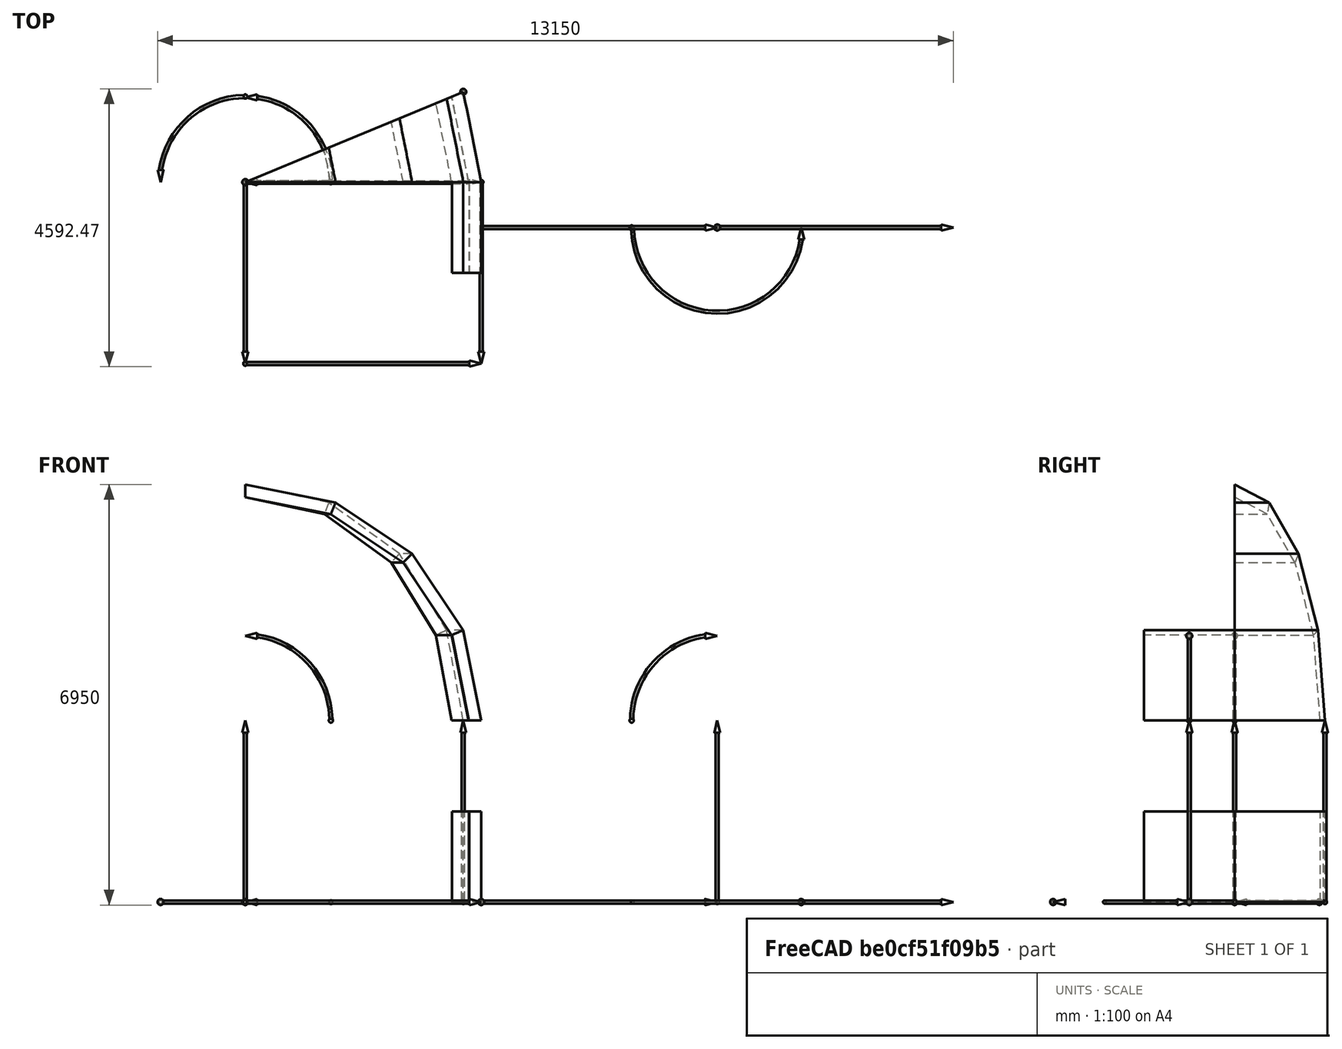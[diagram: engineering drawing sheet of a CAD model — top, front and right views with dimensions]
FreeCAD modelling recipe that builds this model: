
FCSTD DOCUMENT  (FreeCAD 0.18R16146 (Git))
Label: principle
License: CreativeCommons Attribution
LicenseURL: http://creativecommons.org/licenses/by/4.0/
objects: Part::Part2DObjectPython×176, Part::Feature×18, Part::Loft×7, Part::Cone×6, Part::MultiFuse×6, Part::RuledSurface×4, Part::Cylinder×4, Part::Sphere×4, Part::Sweep×2, Part::Box×2, Part::Cut×2
note: 231 computed .brp shape members not serialized (recipe doc carries the construction recipe); baked Part::Feature solids carry a one-line shape summary decoded from their .brp

FEATURE [Part::Part2DObjectPython] Line  # Draft 2D object (typed FeaturePython)
  ChamferSize = 0
  Closed = false
  End = (3900,0,1500)
  FilletRadius = 0
  Length = 1500
  MakeFace = false
  Points = (2) [(3900,0,0),(3900,0,1500)]
  Start = (3900,0,0)
  Subdivisions = 0
FEATURE [Part::Part2DObjectPython] Line001  # Draft 2D object (typed FeaturePython)
  ChamferSize = 0
  Closed = false
  End = (3603.13,0,4492.47)
  FilletRadius = 0
  Length = 1521.7
  MakeFace = false
  Points = (2) [(3900,0,3000),(3603.13,0,4492.47)]
  Start = (3900,0,3000)
  Subdivisions = 0
FEATURE [Part::Part2DObjectPython] Line002  # Draft 2D object (typed FeaturePython)
  ChamferSize = 0
  Closed = false
  End = (3696.08,0,1500)
  FilletRadius = 0
  Length = 1500
  MakeFace = false
  Points = (2) [(3696.08,0,0),(3696.08,0,1500)]
  Start = (3696.08,0,0)
  Subdivisions = 0
FEATURE [Part::Part2DObjectPython] Line003  # Draft 2D object (typed FeaturePython)
  ChamferSize = 0
  Closed = false
  End = (3414.73,0,4414.43)
  FilletRadius = 0
  Length = 1442.14
  MakeFace = false
  Points = (2) [(3696.08,0,3000),(3414.73,0,4414.43)]
  Start = (3696.08,0,3000)
  Subdivisions = 0
FEATURE [Part::Part2DObjectPython] Line004  # Draft 2D object (typed FeaturePython)
  ChamferSize = 0
  Closed = false
  End = (3700,0,1500)
  FilletRadius = 0
  Length = 1500
  MakeFace = false
  Points = (2) [(3700,0,0),(3700,0,1500)]
  Start = (3700,0,0)
  Subdivisions = 0
FEATURE [Part::Part2DObjectPython] Line005  # Draft 2D object (typed FeaturePython)
  ChamferSize = 0
  Closed = false
  End = (3411.04,0,4412.9)
  FilletRadius = 0
  Length = 1440.58
  MakeFace = false
  Points = (2) [(3692.09,0,3000),(3411.04,0,4412.9)]
  Start = (3692.09,0,3000)
  Subdivisions = 0
FEATURE [Part::Part2DObjectPython] Line010  # Draft 2D object (typed FeaturePython)
  ChamferSize = 0
  Closed = false
  End = (-200,-4.44e-14,0)
  FilletRadius = 0
  Length = 200
  MakeFace = false
  Placement = pos=(0,0,0) rot=(0,0,-1;1.5708rad)
  Points = (2) [(0,0,0),(0,-200,0)]
  Start = (0,0,0)
  Subdivisions = 0
FEATURE [Part::Part2DObjectPython] Line012  # Draft 2D object (typed FeaturePython)
  ChamferSize = 0
  Closed = false
  End = (0,-3200,0)
  FilletRadius = 0
  Length = 200
  MakeFace = false
  Placement = pos=(0,-3000,0) rot=(0,0,1;0rad)
  Points = (2) [(0,0,0),(0,-200,0)]
  Start = (0,-3000,0)
  Subdivisions = 0
FEATURE [Part::Part2DObjectPython] Line015  # Draft 2D object (typed FeaturePython)
  ChamferSize = 0
  Closed = false
  End = (-200,-3000,0)
  FilletRadius = 0
  Length = 200
  MakeFace = false
  Placement = pos=(0,-3000,0) rot=(0,0,-1;1.5708rad)
  Points = (2) [(0,0,0),(0,-200,0)]
  Start = (0,-3000,0)
  Subdivisions = 0
FEATURE [Part::RuledSurface] Surface
  Curve1 = -> Line001 [Edge1]
  Curve2 = -> Line003 [Edge1]
  Orientation = 0
FEATURE [Part::RuledSurface] Surface001
  Curve1 = -> Line001 [Edge1]
  Curve2 = -> Line005 [Edge1]
  Orientation = 0
FEATURE [Part::RuledSurface] Surface002
  Curve1 = -> Line [Edge1]
  Curve2 = -> Line002 [Edge1]
  Orientation = 0
FEATURE [Part::RuledSurface] Surface003
  Curve1 = -> Line [Edge1]
  Curve2 = -> Line004 [Edge1]
  Orientation = 0
FEATURE [Part::Feature] Surface004
  Placement = pos=(0,0,0) rot=(0,0,1;0.392699rad)
  shape: bbox 188.4 x 78.04 x 1500 mm, 1 faces, 0 solids (baked)
FEATURE [Part::Loft] Loft
  Closed = false
  MaxDegree = 5
  Ruled = false
  Sections = -> [Surface002,Surface004]
  Solid = true
FEATURE [Part::Feature] Surface005
  Placement = pos=(0,-1500,0) rot=(0,0,1;0rad)
  shape: bbox 200 x 2e-07 x 1500 mm, 1 faces, 0 solids (baked)
FEATURE [Part::Loft] Loft001
  Closed = false
  MaxDegree = 5
  Ruled = false
  Sections = -> [Surface003,Surface005]
  Solid = true
FEATURE [Part::Feature] Surface006
  Placement = pos=(1148.05,0,228.361) rot=(0,-1,0;0.392699rad)
  shape: bbox 992.4 x 2e-07 x 1345 mm, 1 faces, 0 solids (baked)
FEATURE [Part::Feature] Surface007
  Placement = pos=(2121.32,0,878.68) rot=(0,-1,0;0.785398rad)
  shape: bbox 1345 x 2e-07 x 992.4 mm, 1 faces, 0 solids (baked)
FEATURE [Part::Feature] Surface008
  Placement = pos=(2771.64,0,1851.95) rot=(0,-1,0;1.1781rad)
  shape: bbox 1492 x 2e-07 x 489 mm, 1 faces, 0 solids (baked)
FEATURE [Part::Feature] Surface009
  Placement = pos=(0,0,0) rot=(0,0,1;0.392699rad)
  shape: bbox 451.7 x 187.1 x 1492 mm, 1 faces, 0 solids (baked)
FEATURE [Part::Feature] Surface010
  Placement = pos=(1060.66,439.34,228.361) rot=(0.139281,-0.700215,0.700215;0.553564rad)
  shape: bbox 916.9 x 379.8 x 1345 mm, 1 faces, 0 solids (baked)
FEATURE [Part::Feature] Surface011
  Placement = pos=(1959.84,811.794,878.68) rot=(0.176494,-0.887296,0.426094;0.873518rad)
  shape: bbox 1242 x 514.6 x 992.4 mm, 1 faces, 0 solids (baked)
FEATURE [Part::Feature] Surface012
  Placement = pos=(2560.66,1060.66,1851.95) rot=(0.187271,-0.941476,0.280271;1.23443rad)
  shape: bbox 1379 x 571.1 x 489 mm, 1 faces, 0 solids (baked)
FEATURE [Part::Loft] Loft002
  Closed = false
  MaxDegree = 5
  Ruled = false
  Sections = -> [Surface001,Surface009]
  Solid = true
FEATURE [Part::Loft] Loft003
  Closed = false
  MaxDegree = 5
  Ruled = false
  Sections = -> [Surface006,Surface010]
  Solid = true
FEATURE [Part::Loft] Loft004
  Closed = false
  MaxDegree = 5
  Ruled = false
  Sections = -> [Surface007,Surface011]
  Solid = true
FEATURE [Part::Loft] Loft005
  Closed = false
  MaxDegree = 5
  Ruled = false
  Sections = -> [Surface008,Surface012]
  Solid = true
FEATURE [Part::Feature] Surface013
  Placement = pos=(0,-1500,0) rot=(0,0,1;0rad)
  shape: bbox 485.3 x 2e-07 x 1492 mm, 1 faces, 0 solids (baked)
FEATURE [Part::Loft] Loft006
  Closed = false
  MaxDegree = 5
  Ruled = false
  Sections = -> [Surface,Surface013]
  Solid = true
FEATURE [Part::Part2DObjectPython] Rectangle  # Draft 2D object (typed FeaturePython)
  ChamferSize = 0
  Columns = 1
  FilletRadius = 0
  Height = 1500
  Length = 1500
  MakeFace = false
  Placement = pos=(3900,-1500,0) rot=(0.57735,0.57735,0.57735;2.0944rad)
  Rows = 1
FEATURE [Part::Part2DObjectPython] Rectangle001  # Draft 2D object (typed FeaturePython)
  ChamferSize = 0
  Columns = 1
  FilletRadius = 0
  Height = 1500
  Length = 1500
  MakeFace = false
  Placement = pos=(3700,-1500,0) rot=(0.57735,0.57735,0.57735;2.0944rad)
  Rows = 1
FEATURE [Part::Part2DObjectPython] Line016  # Draft 2D object (typed FeaturePython)
  ChamferSize = 0
  Closed = false
  End = (3900,-1500,0)
  FilletRadius = 0
  Length = 200
  MakeFace = true
  Placement = pos=(3700,-1500,0) rot=(0.57735,0.57735,0.57735;2.0944rad)
  Points = (2) [(0,0,0),(0,0,200)]
  Start = (3700,-1500,0)
  Subdivisions = 0
  Support = -> [Loft]
FEATURE [Part::Part2DObjectPython] Line017  # Draft 2D object (typed FeaturePython)
  ChamferSize = 0
  Closed = false
  End = (3900,-1500,1500)
  FilletRadius = 0
  Length = 200
  MakeFace = true
  Placement = pos=(3700,-1500,1500) rot=(0.57735,0.57735,0.57735;2.0944rad)
  Points = (2) [(0,0,0),(0,0,200)]
  Start = (3700,-1500,1500)
  Subdivisions = 0
FEATURE [Part::Part2DObjectPython] Wire001  # Draft 2D object (typed FeaturePython)
  ChamferSize = 0
  Closed = true
  End = (3696.08,0,3000)
  FilletRadius = 0
  Length = 5883.51
  MakeFace = false
  Placement = pos=(3411.04,0,4412.9) rot=(0.57735,0.57735,0.57735;2.0944rad)
  Points = (4) [(0,0,0),(-1500,1.52882,3.69089),(-1500,-1412.9,285.038),(0,-1412.9,285.038)]
  Start = (3411.04,0,4412.9)
  Subdivisions = 0
FEATURE [Part::Part2DObjectPython] Line018  # Draft 2D object (typed FeaturePython)
  ChamferSize = 0
  Closed = false
  End = (3603.13,-1500,4492.47)
  FilletRadius = 0
  Length = 203.918
  MakeFace = true
  Placement = pos=(3414.73,-1500,4414.43) rot=(0.57735,0.57735,0.57735;2.0944rad)
  Points = (2) [(0,0,0),(0,78.0361,188.396)]
  Start = (3414.73,-1500,4414.43)
  Subdivisions = 0
  Support = -> [Loft006]
FEATURE [Part::Part2DObjectPython] Line019  # Draft 2D object (typed FeaturePython)
  ChamferSize = 0
  Closed = false
  End = (3900,-1500,3000)
  FilletRadius = 0
  Length = 203.918
  MakeFace = true
  Placement = pos=(3696.08,-1500,3000) rot=(0.57735,0.57735,0.57735;2.0944rad)
  Points = (2) [(0,0,0),(0,0,203.918)]
  Start = (3696.08,-1500,3000)
  Subdivisions = 0
FEATURE [Part::Cylinder] Cylinder  label="Цилиндр"
  Angle = 360
  AttacherType = Attacher::AttachEngine3D
  Height = 3700
  Placement = pos=(0,0,0) rot=(0,1,0;1.5708rad)
  Radius = 25
FEATURE [Part::Sphere] Sphere  label="Сфера"
  Angle1 = -90
  Angle2 = 90
  Angle3 = 360
  AttacherType = Attacher::AttachEngine3D
  Radius = 35
FEATURE [Part::Cone] Cone  label="Конус"
  Angle = 360
  AttacherType = Attacher::AttachEngine3D
  Height = 200
  Placement = pos=(3700,0,0) rot=(0,1,0;1.5708rad)
  Radius1 = 50
  Radius2 = 0
FEATURE [Part::MultiFuse] Fusion  label="OR"
  Placement = pos=(0,0,-4.17e-13) rot=(0,0,1;0rad)
  Refine = true
  Shapes = -> [Cylinder,Sphere,Cone]
FEATURE [Part::Cone] Cone001  label="Конус001"
  Angle = 360
  AttacherType = Attacher::AttachEngine3D
  Height = 200
  Placement = pos=(2800,0,0) rot=(0,1,0;1.5708rad)
  Radius1 = 50
  Radius2 = 0
FEATURE [Part::Sphere] Sphere001  label="Сфера001"
  Angle1 = -90
  Angle2 = 90
  Angle3 = 360
  AttacherType = Attacher::AttachEngine3D
  Radius = 35
FEATURE [Part::Cylinder] Cylinder001  label="Цилиндр001"
  Angle = 360
  AttacherType = Attacher::AttachEngine3D
  Height = 2800
  Placement = pos=(0,0,0) rot=(0,1,0;1.5708rad)
  Radius = 25
FEATURE [Part::MultiFuse] Fusion001  label="H1"
  Placement = pos=(3603.13,1492.47,0) rot=(0.19148,-0.962637,0.19148;1.60887rad)
  Refine = true
  Shapes = -> [Cylinder001,Sphere001,Cone001]
FEATURE [Part::Cone] Cone002  label="Конус002"
  Angle = 360
  AttacherType = Attacher::AttachEngine3D
  Height = 200
  Placement = pos=(2800,0,0) rot=(0,1,0;1.5708rad)
  Radius1 = 50
  Radius2 = 0
FEATURE [Part::Sphere] Sphere002  label="Сфера002"
  Angle1 = -90
  Angle2 = 90
  Angle3 = 360
  AttacherType = Attacher::AttachEngine3D
  Radius = 35
FEATURE [Part::Cylinder] Cylinder002  label="Цилиндр002"
  Angle = 360
  AttacherType = Attacher::AttachEngine3D
  Height = 2800
  Placement = pos=(0,0,0) rot=(0,1,0;1.5708rad)
  Radius = 25
FEATURE [Part::MultiFuse] Fusion002  label="LONG"
  Placement = pos=(0,0,0) rot=(0,0,-1;1.5708rad)
  Refine = true
  Shapes = -> [Cylinder002,Sphere002,Cone002]
FEATURE [Part::Sphere] Sphere003  label="Сфера003"
  Angle1 = -90
  Angle2 = 90
  Angle3 = 360
  AttacherType = Attacher::AttachEngine3D
  Placement = pos=(1415,0,0) rot=(0,0,1;0rad)
  Radius = 35
FEATURE [Part::Part2DObjectPython] Circle001  # Draft 2D object (typed FeaturePython)
  FirstAngle = 0
  LastAngle = 0
  MakeFace = true
  Placement = pos=(1415,0,0) rot=(1,0,0;1.5708rad)
  Radius = 25
FEATURE [Part::Part2DObjectPython] Arc  # Draft 2D object (typed FeaturePython)
  FirstAngle = 0
  LastAngle = 90
  MakeFace = true
  Radius = 1415
FEATURE [Part::Sweep] Sweep
  Frenet = false
  Sections = -> [Circle001]
  Solid = true
  Spine = -> Arc [Edge1]
  Transition = 1
FEATURE [Part::Cone] Cone003  label="Конус003"
  Angle = 360
  AttacherType = Attacher::AttachEngine3D
  Height = 200
  Placement = pos=(200,1400,0) rot=(0,-1,0;1.5708rad)
  Radius1 = 50
  Radius2 = 0
FEATURE [Part::Feature] Fusion004  label="H002"
  Placement = pos=(0,0,0) rot=(0.19148,-0.962637,0.19148;1.60887rad)
  shape: bbox 100 x 100 x 3035 mm, 4 faces (baked)
FEATURE [Part::Feature] Fusion006  label="OR001"
  Placement = pos=(0,-3000,-4.17e-13) rot=(0,0,1;0rad)
  shape: bbox 3935 x 100 x 100 mm, 4 faces (baked)
FEATURE [Part::Feature] Fusion007  label="LONG001"
  Placement = pos=(3900,0,0) rot=(0,0,-1;1.5708rad)
  shape: bbox 100 x 3035 x 100 mm, 4 faces (baked)
FEATURE [Part::Part2DObjectPython] Line021  # Draft 2D object (typed FeaturePython)
  ChamferSize = 0
  Closed = false
  End = (3900,0,3000)
  FilletRadius = 0
  Length = 3900
  MakeFace = true
  Placement = pos=(6.251e-13,-3.501e-13,3000) rot=(0,0,1;0rad)
  Points = (2) [(0,0,0),(3900,2.30658e-13,4.54747e-13)]
  Start = (6.251e-13,-3.501e-13,3000)
  Subdivisions = 0
FEATURE [Part::Part2DObjectPython] Line025  # Draft 2D object (typed FeaturePython)
  ChamferSize = 0
  Closed = false
  End = (3900,0,0)
  FilletRadius = 0
  Length = 3000
  MakeFace = true
  Placement = pos=(3900,0,3000) rot=(0,0,1;0rad)
  Points = (2) [(0,0,0),(0,0,-3000)]
  Start = (3900,0,3000)
  Subdivisions = 0
FEATURE [Part::Part2DObjectPython] Line026  # Draft 2D object (typed FeaturePython)
  ChamferSize = 0
  Closed = false
  End = (3603.13,1492.47,0)
  FilletRadius = 0
  Length = 1521.7
  MakeFace = true
  Placement = pos=(3900,0,0) rot=(0,0,1;0rad)
  Points = (2) [(0,0,0),(-296.87,1492.47,0)]
  Start = (3900,0,0)
  Subdivisions = 0
  Support = -> [Loft]
FEATURE [Part::Part2DObjectPython] Line027  # Draft 2D object (typed FeaturePython)
  ChamferSize = 0
  Closed = false
  End = (2757.72,2757.72,0)
  FilletRadius = 0
  Length = 1521.7
  MakeFace = true
  Placement = pos=(3603.13,1492.47,0) rot=(0,0,1;0.392699rad)
  Points = (2) [(0,0,0),(-296.87,1492.47,0)]
  Start = (3603.13,1492.47,0)
  Subdivisions = 0
  Support = -> [Loft]
FEATURE [Part::Part2DObjectPython] Line028  # Draft 2D object (typed FeaturePython)
  ChamferSize = 0
  Closed = false
  End = (1492.47,3603.13,0)
  FilletRadius = 0
  Length = 1521.7
  MakeFace = true
  Placement = pos=(2757.72,2757.72,0) rot=(0,0,1;0.785398rad)
  Points = (2) [(0,0,0),(-296.87,1492.47,0)]
  Start = (2757.72,2757.72,0)
  Subdivisions = 0
  Support = -> [Loft]
FEATURE [Part::Part2DObjectPython] Line029  # Draft 2D object (typed FeaturePython)
  ChamferSize = 0
  Closed = false
  End = (-4.3201e-12,3900,0)
  FilletRadius = 0
  Length = 1521.7
  MakeFace = true
  Placement = pos=(1492.47,3603.13,0) rot=(0,0,1;1.1781rad)
  Points = (2) [(0,0,0),(-296.87,1492.47,0)]
  Start = (1492.47,3603.13,0)
  Subdivisions = 0
  Support = -> [Loft]
FEATURE [Part::Box] Box  label="Куб"
  AttacherType = Attacher::AttachEngine3D
  Height = 60
  Length = 200
  Placement = pos=(0,1300,-30) rot=(0,0,1;0rad)
  Width = 200
FEATURE [Part::Cut] Cut
  Base = -> Sweep
  Refine = true
  Tool = -> Box
FEATURE [Part::MultiFuse] Fusion010  label="TORSION"
  Refine = true
  Shapes = -> [Cut,Sphere003,Cone003]
FEATURE [Part::Part2DObjectPython] Line030  # Draft 2D object (typed FeaturePython)
  ChamferSize = 0
  Closed = false
  End = (3603.13,1492.47,0)
  FilletRadius = 0
  Length = 3900
  MakeFace = true
  Points = (2) [(0,0,0),(3603.13,1492.47,0)]
  Start = (0,0,0)
  Subdivisions = 0
FEATURE [Part::Part2DObjectPython] Line031  # Draft 2D object (typed FeaturePython)
  ChamferSize = 0
  Closed = false
  End = (2757.72,2757.72,0)
  FilletRadius = 0
  Length = 3900
  MakeFace = true
  Placement = pos=(0,0,0) rot=(0,0,1;0.392699rad)
  Points = (2) [(0,0,0),(3603.13,1492.47,0)]
  Start = (0,0,0)
  Subdivisions = 0
FEATURE [Part::Part2DObjectPython] Line032  # Draft 2D object (typed FeaturePython)
  ChamferSize = 0
  Closed = false
  End = (1492.47,3603.13,0)
  FilletRadius = 0
  Length = 3900
  MakeFace = true
  Placement = pos=(0,0,0) rot=(0,0,1;0.785398rad)
  Points = (2) [(0,0,0),(3603.13,1492.47,0)]
  Start = (0,0,0)
  Subdivisions = 0
FEATURE [Part::Part2DObjectPython] Line033  # Draft 2D object (typed FeaturePython)
  ChamferSize = 0
  Closed = false
  End = (3603.13,-1.193e-13,4492.47)
  FilletRadius = 0
  Length = 3900
  MakeFace = true
  Placement = pos=(9.09e-13,-3.5e-13,3000) rot=(0,-1,0;0.392699rad)
  Points = (2) [(0,0,0),(3900,2.30658e-13,2.27374e-12)]
  Start = (9.09e-13,-3.5e-13,3000)
  Subdivisions = 0
FEATURE [Part::Part2DObjectPython] Line034  # Draft 2D object (typed FeaturePython)
  ChamferSize = 0
  Closed = false
  End = (2757.72,-1.193e-13,5757.72)
  FilletRadius = 0
  Length = 3900
  MakeFace = true
  Placement = pos=(9.09e-13,-3.5e-13,3000) rot=(0,-1,0;0.785398rad)
  Points = (2) [(0,0,0),(3900,2.30658e-13,-4.54747e-13)]
  Start = (9.09e-13,-3.5e-13,3000)
  Subdivisions = 0
FEATURE [Part::Part2DObjectPython] Line035  # Draft 2D object (typed FeaturePython)
  ChamferSize = 0
  Closed = false
  End = (2757.72,-1.193e-13,5757.72)
  FilletRadius = 0
  Length = 3900
  MakeFace = true
  Placement = pos=(6.82e-13,-3.5e-13,3000) rot=(0,-1,0;1.1781rad)
  Points = (2) [(-2.27374e-12,-1e-16,4.54747e-13),(3603.13,2.30658e-13,-1492.47)]
  Start = (-3.982e-13,-3.501e-13,3000)
  Subdivisions = 0
FEATURE [Part::Feature] Fusion011  label="TORSION001"
  Placement = pos=(6.251e-13,-3.501e-13,3000) rot=(1,0,0;1.5708rad)
  shape: bbox 1558 x 100 x 1579 mm, 4 faces (baked)
FEATURE [Part::Feature] Fusion012  label="TORSION002"
  Placement = pos=(0,0,0) rot=(0,0,1;1.5708rad)
  shape: bbox 1579 x 1558 x 100 mm, 4 faces (baked)
FEATURE [Part::Part2DObjectPython] Line036  # Draft 2D object (typed FeaturePython)
  ChamferSize = 0
  Closed = false
  End = (2757.72,-1.193e-13,5757.72)
  FilletRadius = 0
  Length = 3900
  MakeFace = true
  Placement = pos=(9.09e-13,-3.5e-13,3000) rot=(0,-1,0;0.785398rad)
  Points = (2) [(0,0,0),(3900,2.30658e-13,3.18323e-12)]
  Start = (9.09e-13,-3.5e-13,3000)
  Subdivisions = 0
FEATURE [Part::Part2DObjectPython] Line037  # Draft 2D object (typed FeaturePython)
  ChamferSize = 0
  Closed = false
  End = (1492.47,-1.193e-13,6603.13)
  FilletRadius = 0
  Length = 3900
  MakeFace = true
  Placement = pos=(9.09e-13,-3.5e-13,3000) rot=(0,-1,0;1.1781rad)
  Points = (2) [(0,0,0),(3900,2.30658e-13,3.41061e-12)]
  Start = (9.09e-13,-3.5e-13,3000)
  Subdivisions = 0
FEATURE [Part::Part2DObjectPython] Line038  # Draft 2D object (typed FeaturePython)
  ChamferSize = 0
  Closed = false
  End = (-2.0896e-12,-1.193e-13,6900)
  FilletRadius = 0
  Length = 3900
  MakeFace = true
  Placement = pos=(4.55e-13,-3.5e-13,3000) rot=(0,-1,0;1.5708rad)
  Points = (2) [(0,0,0),(3900,2.30658e-13,3.41061e-12)]
  Start = (4.55e-13,-3.5e-13,3000)
  Subdivisions = 0
FEATURE [Part::Part2DObjectPython] Line039  # Draft 2D object (typed FeaturePython)
  ChamferSize = 0
  Closed = false
  End = (-1.5916e-12,3900,0)
  FilletRadius = 0
  Length = 3900
  MakeFace = true
  Placement = pos=(0,0,0) rot=(0,0,1;1.1781rad)
  Points = (2) [(0,0,0),(3603.13,1492.47,0)]
  Start = (0,0,0)
  Subdivisions = 0
FEATURE [Part::Part2DObjectPython] Line040  # Draft 2D object (typed FeaturePython)
  ChamferSize = 0
  Closed = false
  End = (3900,0,1500)
  FilletRadius = 0
  Length = 1500
  MakeFace = false
  Points = (2) [(3900,0,0),(3900,0,1500)]
  Start = (3900,0,0)
  Subdivisions = 0
FEATURE [Part::Part2DObjectPython] Line041  # Draft 2D object (typed FeaturePython)
  ChamferSize = 0
  Closed = false
  End = (4196.87,0,4492.47)
  FilletRadius = 0
  Length = 1521.7
  MakeFace = false
  Points = (2) [(3900,0,3000),(4196.87,0,4492.47)]
  Start = (3900,0,3000)
  Subdivisions = 0
FEATURE [Part::Part2DObjectPython] Line042  # Draft 2D object (typed FeaturePython)
  ChamferSize = 0
  Closed = false
  End = (4103.92,0,1500)
  FilletRadius = 0
  Length = 1500
  MakeFace = false
  Points = (2) [(4103.92,0,0),(4103.92,0,1500)]
  Start = (4103.92,0,0)
  Subdivisions = 0
FEATURE [Part::Part2DObjectPython] Line043  # Draft 2D object (typed FeaturePython)
  ChamferSize = 0
  Closed = false
  End = (4385.27,0,4414.43)
  FilletRadius = 0
  Length = 1442.14
  MakeFace = false
  Points = (2) [(4103.92,0,3000),(4385.27,0,4414.43)]
  Start = (4103.92,0,3000)
  Subdivisions = 0
FEATURE [Part::Part2DObjectPython] Line044  # Draft 2D object (typed FeaturePython)
  ChamferSize = 0
  Closed = false
  End = (4100,0,1500)
  FilletRadius = 0
  Length = 1500
  MakeFace = false
  Points = (2) [(4100,0,0),(4100,0,1500)]
  Start = (4100,0,0)
  Subdivisions = 0
FEATURE [Part::Part2DObjectPython] Line045  # Draft 2D object (typed FeaturePython)
  ChamferSize = 0
  Closed = false
  End = (4388.96,0,4412.9)
  FilletRadius = 0
  Length = 1440.58
  MakeFace = false
  Points = (2) [(4107.91,0,3000),(4388.96,0,4412.9)]
  Start = (4107.91,0,3000)
  Subdivisions = 0
FEATURE [Part::Part2DObjectPython] Line056  # Draft 2D object (typed FeaturePython)
  ChamferSize = 0
  Closed = false
  End = (11700,0,1500)
  FilletRadius = 0
  Length = 1500
  MakeFace = false
  Points = (2) [(11700,0,0),(11700,0,1500)]
  Start = (11700,0,0)
  Subdivisions = 0
FEATURE [Part::Part2DObjectPython] Line057  # Draft 2D object (typed FeaturePython)
  ChamferSize = 0
  Closed = false
  End = (11403.1,0,4492.47)
  FilletRadius = 0
  Length = 1521.7
  MakeFace = false
  Points = (2) [(11700,0,3000),(11403.1,0,4492.47)]
  Start = (11700,0,3000)
  Subdivisions = 0
FEATURE [Part::Part2DObjectPython] Line058  # Draft 2D object (typed FeaturePython)
  ChamferSize = 0
  Closed = false
  End = (11496.1,0,1500)
  FilletRadius = 0
  Length = 1500
  MakeFace = false
  Points = (2) [(11496.1,0,0),(11496.1,0,1500)]
  Start = (11496.1,0,0)
  Subdivisions = 0
FEATURE [Part::Part2DObjectPython] Line059  # Draft 2D object (typed FeaturePython)
  ChamferSize = 0
  Closed = false
  End = (11214.7,0,4414.43)
  FilletRadius = 0
  Length = 1442.14
  MakeFace = false
  Points = (2) [(11496.1,0,3000),(11214.7,0,4414.43)]
  Start = (11496.1,0,3000)
  Subdivisions = 0
FEATURE [Part::Part2DObjectPython] Line060  # Draft 2D object (typed FeaturePython)
  ChamferSize = 0
  Closed = false
  End = (11500,0,1500)
  FilletRadius = 0
  Length = 1500
  MakeFace = false
  Points = (2) [(11500,0,0),(11500,0,1500)]
  Start = (11500,0,0)
  Subdivisions = 0
FEATURE [Part::Part2DObjectPython] Line061  # Draft 2D object (typed FeaturePython)
  ChamferSize = 0
  Closed = false
  End = (11211,0,4412.9)
  FilletRadius = 0
  Length = 1440.58
  MakeFace = false
  Points = (2) [(11492.1,0,3000),(11211,0,4412.9)]
  Start = (11492.1,0,3000)
  Subdivisions = 0
FEATURE [Part::Part2DObjectPython] Line062  # Draft 2D object (typed FeaturePython)
  ChamferSize = 0
  Closed = false
  End = (4196.87,-1500,4492.47)
  FilletRadius = 0
  Length = 1521.7
  MakeFace = false
  Placement = pos=(0,-1500,0) rot=(0,0,1;0rad)
  Points = (2) [(3900,0,3000),(4196.87,0,4492.47)]
  Start = (3900,-1500,3000)
  Subdivisions = 0
FEATURE [Part::Part2DObjectPython] Line063  # Draft 2D object (typed FeaturePython)
  ChamferSize = 0
  Closed = false
  End = (11403.1,-1500,4492.47)
  FilletRadius = 0
  Length = 1521.7
  MakeFace = false
  Placement = pos=(0,-1500,0) rot=(0,0,1;0rad)
  Points = (2) [(11700,0,3000),(11403.1,0,4492.47)]
  Start = (11700,-1500,3000)
  Subdivisions = 0
FEATURE [Part::Part2DObjectPython] Line064  # Draft 2D object (typed FeaturePython)
  ChamferSize = 0
  Closed = false
  End = (4385.27,-1500,4414.43)
  FilletRadius = 0
  Length = 1442.14
  MakeFace = false
  Placement = pos=(0,-1500,0) rot=(0,0,1;0rad)
  Points = (2) [(4103.92,0,3000),(4385.27,0,4414.43)]
  Start = (4103.92,-1500,3000)
  Subdivisions = 0
FEATURE [Part::Part2DObjectPython] Line065  # Draft 2D object (typed FeaturePython)
  ChamferSize = 0
  Closed = false
  End = (11214.7,-1500,4414.43)
  FilletRadius = 0
  Length = 1442.14
  MakeFace = false
  Placement = pos=(0,-1500,0) rot=(0,0,1;0rad)
  Points = (2) [(11496.1,0,3000),(11214.7,0,4414.43)]
  Start = (11496.1,-1500,3000)
  Subdivisions = 0
FEATURE [Part::Part2DObjectPython] Line066  # Draft 2D object (typed FeaturePython)
  ChamferSize = 0
  Closed = false
  End = (4100,-1500,1500)
  FilletRadius = 0
  Length = 1500
  MakeFace = false
  Placement = pos=(0,-1500,0) rot=(0,0,1;0rad)
  Points = (2) [(4100,0,0),(4100,0,1500)]
  Start = (4100,-1500,0)
  Subdivisions = 0
FEATURE [Part::Part2DObjectPython] Line067  # Draft 2D object (typed FeaturePython)
  ChamferSize = 0
  Closed = false
  End = (11700,-1500,1500)
  FilletRadius = 0
  Length = 1500
  MakeFace = false
  Placement = pos=(0,-1500,0) rot=(0,0,1;0rad)
  Points = (2) [(11700,0,0),(11700,0,1500)]
  Start = (11700,-1500,0)
  Subdivisions = 0
FEATURE [Part::Part2DObjectPython] Line068  # Draft 2D object (typed FeaturePython)
  ChamferSize = 0
  Closed = false
  End = (11500,-1500,1500)
  FilletRadius = 0
  Length = 1500
  MakeFace = false
  Placement = pos=(0,-1500,0) rot=(0,0,1;0rad)
  Points = (2) [(11500,0,0),(11500,0,1500)]
  Start = (11500,-1500,0)
  Subdivisions = 0
FEATURE [Part::Part2DObjectPython] Line069  # Draft 2D object (typed FeaturePython)
  ChamferSize = 0
  Closed = false
  End = (3900,-1500,1500)
  FilletRadius = 0
  Length = 200
  MakeFace = true
  Placement = pos=(4100,-1500,1500) rot=(0,0,1;0rad)
  Points = (2) [(0,0,0),(-200,0,0)]
  Start = (4100,-1500,1500)
  Subdivisions = 0
FEATURE [Part::Part2DObjectPython] Line070  # Draft 2D object (typed FeaturePython)
  ChamferSize = 0
  Closed = false
  End = (3900,-1500,0)
  FilletRadius = 0
  Length = 200
  MakeFace = true
  Placement = pos=(4100,-1500,0) rot=(0,0,1;0rad)
  Points = (2) [(0,0,0),(-200,0,0)]
  Start = (4100,-1500,0)
  Subdivisions = 0
FEATURE [Part::Part2DObjectPython] Line071  # Draft 2D object (typed FeaturePython)
  ChamferSize = 0
  Closed = false
  End = (4100,0,0)
  FilletRadius = 0
  Length = 1500
  MakeFace = true
  Placement = pos=(4100,-1500,0) rot=(0,0,1;0rad)
  Points = (2) [(0,0,0),(0,1500,0)]
  Start = (4100,-1500,0)
  Subdivisions = 0
FEATURE [Part::Part2DObjectPython] Line072  # Draft 2D object (typed FeaturePython)
  ChamferSize = 0
  Closed = false
  End = (4100,0,1500)
  FilletRadius = 0
  Length = 1500
  MakeFace = true
  Placement = pos=(4100,-1500,1500) rot=(0,0,1;0rad)
  Points = (2) [(0,0,0),(0,1500,0)]
  Start = (4100,-1500,1500)
  Subdivisions = 0
FEATURE [Part::Part2DObjectPython] Line073  # Draft 2D object (typed FeaturePython)
  ChamferSize = 0
  Closed = false
  End = (3900,0,1500)
  FilletRadius = 0
  Length = 200
  MakeFace = true
  Placement = pos=(4100,0,1500) rot=(0,0,1;0rad)
  Points = (2) [(0,0,0),(-200,6.12323e-15,0)]
  Start = (4100,0,1500)
  Subdivisions = 0
FEATURE [Part::Part2DObjectPython] Line074  # Draft 2D object (typed FeaturePython)
  ChamferSize = 0
  Closed = false
  End = (11700,0,1500)
  FilletRadius = 0
  Length = 1500
  MakeFace = true
  Placement = pos=(11700,-1500,1500) rot=(0,0,1;0rad)
  Points = (2) [(0,0,0),(0,1500,0)]
  Start = (11700,-1500,1500)
  Subdivisions = 0
FEATURE [Part::Part2DObjectPython] Line075  # Draft 2D object (typed FeaturePython)
  ChamferSize = 0
  Closed = false
  End = (11500,0,1500)
  FilletRadius = 0
  Length = 1500
  MakeFace = true
  Placement = pos=(11500,-1500,1500) rot=(0,0,1;0rad)
  Points = (2) [(0,0,0),(0,1500,0)]
  Start = (11500,-1500,1500)
  Subdivisions = 0
FEATURE [Part::Part2DObjectPython] Line076  # Draft 2D object (typed FeaturePython)
  ChamferSize = 0
  Closed = false
  End = (11700,0,0)
  FilletRadius = 0
  Length = 1500
  MakeFace = true
  Placement = pos=(11700,-1500,0) rot=(0,0,1;0rad)
  Points = (2) [(0,0,0),(0,1500,0)]
  Start = (11700,-1500,0)
  Subdivisions = 0
FEATURE [Part::Part2DObjectPython] Line077  # Draft 2D object (typed FeaturePython)
  ChamferSize = 0
  Closed = false
  End = (11500,0,0)
  FilletRadius = 0
  Length = 1500
  MakeFace = true
  Placement = pos=(11500,-1500,0) rot=(0,0,1;0rad)
  Points = (2) [(0,0,0),(0,1500,0)]
  Start = (11500,-1500,0)
  Subdivisions = 0
FEATURE [Part::Part2DObjectPython] Line078  # Draft 2D object (typed FeaturePython)
  ChamferSize = 0
  Closed = false
  End = (11700,0,1500)
  FilletRadius = 0
  Length = 200
  MakeFace = true
  Placement = pos=(11500,0,1500) rot=(0,0,1;0rad)
  Points = (2) [(0,0,0),(200,-6.12323e-15,0)]
  Start = (11500,0,1500)
  Subdivisions = 0
FEATURE [Part::Part2DObjectPython] Line079  # Draft 2D object (typed FeaturePython)
  ChamferSize = 0
  Closed = false
  End = (11500,-1500,1500)
  FilletRadius = 0
  Length = 200
  MakeFace = true
  Placement = pos=(11700,-1500,1500) rot=(0,0,1;0rad)
  Points = (2) [(0,0,0),(-200,0,0)]
  Start = (11700,-1500,1500)
  Subdivisions = 0
FEATURE [Part::Part2DObjectPython] Line080  # Draft 2D object (typed FeaturePython)
  ChamferSize = 0
  Closed = false
  End = (11500,-1500,0)
  FilletRadius = 0
  Length = 200
  MakeFace = true
  Placement = pos=(11700,-1500,0) rot=(0,0,1;0rad)
  Points = (2) [(0,0,0),(-200,0,0)]
  Start = (11700,-1500,0)
  Subdivisions = 0
FEATURE [Part::Part2DObjectPython] Line081  # Draft 2D object (typed FeaturePython)
  ChamferSize = 0
  Closed = false
  End = (11500,0,0)
  FilletRadius = 0
  Length = 200
  MakeFace = true
  Placement = pos=(11700,0,0) rot=(0,0,1;0rad)
  Points = (2) [(0,0,0),(-200,6.12323e-15,0)]
  Start = (11700,0,0)
  Subdivisions = 0
FEATURE [Part::Part2DObjectPython] Line082  # Draft 2D object (typed FeaturePython)
  ChamferSize = 0
  Closed = false
  End = (11403.1,0,4492.47)
  FilletRadius = 0
  Length = 1500
  MakeFace = true
  Placement = pos=(11403.1,-1500,4492.47) rot=(0,0,1;0rad)
  Points = (2) [(0,0,0),(0,1500,0)]
  Start = (11403.1,-1500,4492.47)
  Subdivisions = 0
FEATURE [Part::Part2DObjectPython] Line083  # Draft 2D object (typed FeaturePython)
  ChamferSize = 0
  Closed = false
  End = (11700,0,3000)
  FilletRadius = 0
  Length = 1500
  MakeFace = true
  Placement = pos=(11700,-1500,3000) rot=(0,0,1;0rad)
  Points = (2) [(0,0,0),(0,1500,0)]
  Start = (11700,-1500,3000)
  Subdivisions = 0
FEATURE [Part::Part2DObjectPython] Line084  # Draft 2D object (typed FeaturePython)
  ChamferSize = 0
  Closed = false
  End = (11496.1,-1500,3000)
  FilletRadius = 0
  Length = 203.918
  MakeFace = true
  Placement = pos=(11700,-1500,3000) rot=(0,0,1;0rad)
  Points = (2) [(0,0,0),(-203.918,0,0)]
  Start = (11700,-1500,3000)
  Subdivisions = 0
FEATURE [Part::Part2DObjectPython] Line085  # Draft 2D object (typed FeaturePython)
  ChamferSize = 0
  Closed = false
  End = (11496.1,0,3000)
  FilletRadius = 0
  Length = 203.918
  MakeFace = true
  Placement = pos=(11700,0,3000) rot=(0,0,1;0rad)
  Points = (2) [(0,0,0),(-203.918,6.2432e-15,0)]
  Start = (11700,0,3000)
  Subdivisions = 0
FEATURE [Part::Part2DObjectPython] Line086  # Draft 2D object (typed FeaturePython)
  ChamferSize = 0
  Closed = false
  End = (11214.7,-1500,4414.43)
  FilletRadius = 0
  Length = 203.918
  MakeFace = true
  Placement = pos=(11403.1,-1500,4492.47) rot=(0,0,1;0rad)
  Points = (2) [(0,0,0),(-188.396,0,-78.0361)]
  Start = (11403.1,-1500,4492.47)
  Subdivisions = 0
FEATURE [Part::Part2DObjectPython] Line087  # Draft 2D object (typed FeaturePython)
  ChamferSize = 0
  Closed = false
  End = (11214.7,0,4414.43)
  FilletRadius = 0
  Length = 203.918
  MakeFace = true
  Placement = pos=(11403.1,0,4492.47) rot=(0,0,1;0rad)
  Points = (2) [(0,0,0),(-188.396,5.76796e-15,-78.0361)]
  Start = (11403.1,0,4492.47)
  Subdivisions = 0
FEATURE [Part::Part2DObjectPython] Line088  # Draft 2D object (typed FeaturePython)
  ChamferSize = 0
  Closed = false
  End = (11214.7,0,4414.43)
  FilletRadius = 0
  Length = 1500
  MakeFace = true
  Placement = pos=(11214.7,-1500,4414.43) rot=(0,0,1;0rad)
  Points = (2) [(0,0,0),(0,1500,0)]
  Start = (11214.7,-1500,4414.43)
  Subdivisions = 0
FEATURE [Part::Part2DObjectPython] Line089  # Draft 2D object (typed FeaturePython)
  ChamferSize = 0
  Closed = false
  End = (11496.1,0,3000)
  FilletRadius = 0
  Length = 1500
  MakeFace = true
  Placement = pos=(11496.1,-1500,3000) rot=(0,0,1;0rad)
  Points = (2) [(0,0,0),(0,1500,0)]
  Start = (11496.1,-1500,3000)
  Subdivisions = 0
FEATURE [Part::Part2DObjectPython] Line090  # Draft 2D object (typed FeaturePython)
  ChamferSize = 0
  Closed = false
  End = (3900,-1500,3000)
  FilletRadius = 0
  Length = 203.918
  MakeFace = true
  Placement = pos=(4103.92,-1500,3000) rot=(0,0,1;0rad)
  Points = (2) [(0,0,0),(-203.918,0,0)]
  Start = (4103.92,-1500,3000)
  Subdivisions = 0
FEATURE [Part::Part2DObjectPython] Line091  # Draft 2D object (typed FeaturePython)
  ChamferSize = 0
  Closed = false
  End = (4196.87,0,4492.47)
  FilletRadius = 0
  Length = 1500
  MakeFace = true
  Placement = pos=(4196.87,-1500,4492.47) rot=(0,0,1;0rad)
  Points = (2) [(0,0,0),(0,1500,0)]
  Start = (4196.87,-1500,4492.47)
  Subdivisions = 0
FEATURE [Part::Part2DObjectPython] Line092  # Draft 2D object (typed FeaturePython)
  ChamferSize = 0
  Closed = false
  End = (4385.27,0,4414.43)
  FilletRadius = 0
  Length = 1500
  MakeFace = true
  Placement = pos=(4385.27,-1500,4414.43) rot=(0,0,1;0rad)
  Points = (2) [(0,0,0),(0,1500,0)]
  Start = (4385.27,-1500,4414.43)
  Subdivisions = 0
FEATURE [Part::Part2DObjectPython] Line094  # Draft 2D object (typed FeaturePython)
  ChamferSize = 0
  Closed = false
  End = (4103.92,0,3000)
  FilletRadius = 0
  Length = 203.918
  MakeFace = true
  Placement = pos=(3900,0,3000) rot=(0,0,1;0rad)
  Points = (2) [(0,0,0),(203.918,-6.2432e-15,0)]
  Start = (3900,0,3000)
  Subdivisions = 0
FEATURE [Part::Part2DObjectPython] Line095  # Draft 2D object (typed FeaturePython)
  ChamferSize = 0
  Closed = false
  End = (4103.92,0,3000)
  FilletRadius = 0
  Length = 1500
  MakeFace = true
  Placement = pos=(4103.92,-1500,3000) rot=(0,0,1;0rad)
  Points = (2) [(0,0,0),(0,1500,0)]
  Start = (4103.92,-1500,3000)
  Subdivisions = 0
FEATURE [Part::Part2DObjectPython] Line096  # Draft 2D object (typed FeaturePython)
  ChamferSize = 0
  Closed = false
  End = (4385.27,-1500,4414.43)
  FilletRadius = 0
  Length = 203.918
  MakeFace = true
  Placement = pos=(4196.87,-1500,4492.47) rot=(0,0,1;0rad)
  Points = (2) [(0,0,0),(188.396,0,-78.0361)]
  Start = (4196.87,-1500,4492.47)
  Subdivisions = 0
FEATURE [Part::Part2DObjectPython] Line097  # Draft 2D object (typed FeaturePython)
  ChamferSize = 0
  Closed = false
  End = (5042.28,0,5757.72)
  FilletRadius = 0
  Length = 1521.7
  MakeFace = false
  Placement = pos=(-554.311,0,3213.29) rot=(0,1,0;0.392699rad)
  Points = (2) [(3900,0,3000),(4196.87,0,4492.47)]
  Start = (4196.87,0,4492.47)
  Subdivisions = 0
FEATURE [Part::Part2DObjectPython] Line100  # Draft 2D object (typed FeaturePython)
  ChamferSize = 0
  Closed = false
  End = (4385.27,-6.2e-15,4414.43)
  FilletRadius = 0
  Length = 203.918
  MakeFace = true
  Placement = pos=(4196.87,0,4492.47) rot=(0,1,0;0.392699rad)
  Points = (2) [(0,0,0),(203.918,-6.2432e-15,-1.81899e-12)]
  Start = (4196.87,0,4492.47)
  Subdivisions = 0
FEATURE [Part::Part2DObjectPython] Line101  # Draft 2D object (typed FeaturePython)
  ChamferSize = 0
  Closed = false
  End = (6307.53,0,6603.13)
  FilletRadius = 0
  Length = 1521.7
  MakeFace = false
  Placement = pos=(163.247,0,6394.11) rot=(0,1,0;0.785398rad)
  Points = (2) [(3900,0,3000),(4196.87,0,4492.47)]
  Start = (5042.28,0,5757.72)
  Subdivisions = 0
FEATURE [Part::Part2DObjectPython] Line102  # Draft 2D object (typed FeaturePython)
  ChamferSize = 0
  Closed = false
  End = (6387.1,0,6411.04)
  FilletRadius = 0
  Length = 1440.58
  MakeFace = false
  Placement = pos=(163.247,0,6394.11) rot=(0,1,0;0.785398rad)
  Points = (2) [(4107.91,0,3000),(4388.96,0,4412.9)]
  Start = (5189.3,0,5610.7)
  Subdivisions = 0
FEATURE [Part::Part2DObjectPython] Line103  # Draft 2D object (typed FeaturePython)
  ChamferSize = 0
  Closed = false
  End = (6385.57,-5.8e-15,6414.73)
  FilletRadius = 0
  Length = 203.918
  MakeFace = true
  Placement = pos=(6307.53,0,6603.13) rot=(0,1,0;0.785398rad)
  Points = (2) [(0,0,0),(188.396,-5.76796e-15,-78.0361)]
  Start = (6307.53,0,6603.13)
  Subdivisions = 0
FEATURE [Part::Part2DObjectPython] Line104  # Draft 2D object (typed FeaturePython)
  ChamferSize = 0
  Closed = false
  End = (5186.48,-6.2e-15,5613.52)
  FilletRadius = 0
  Length = 203.918
  MakeFace = true
  Placement = pos=(5042.28,0,5757.72) rot=(0,1,0;0.785398rad)
  Points = (2) [(0,0,0),(203.918,-6.2432e-15,0)]
  Start = (5042.28,0,5757.72)
  Subdivisions = 0
FEATURE [Part::Part2DObjectPython] Line105  # Draft 2D object (typed FeaturePython)
  ChamferSize = 0
  Closed = false
  End = (7800,0,6900)
  FilletRadius = 0
  Length = 1521.7
  MakeFace = false
  Placement = pos=(2043.43,0,9058.21) rot=(0,1,0;1.1781rad)
  Points = (2) [(3900,0,3000),(4196.87,0,4492.47)]
  Start = (6307.53,0,6603.13)
  Subdivisions = 0
FEATURE [Part::Part2DObjectPython] Line106  # Draft 2D object (typed FeaturePython)
  ChamferSize = 0
  Closed = false
  End = (7800,0,6692.09)
  FilletRadius = 0
  Length = 1440.58
  MakeFace = false
  Placement = pos=(2043.43,0,9058.21) rot=(0,1,0;1.1781rad)
  Points = (2) [(4107.91,0,3000),(4388.96,0,4412.9)]
  Start = (6387.1,0,6411.04)
  Subdivisions = 0
FEATURE [Part::Part2DObjectPython] Line107  # Draft 2D object (typed FeaturePython)
  ChamferSize = 0
  Closed = false
  End = (7800,-5.8e-15,6696.08)
  FilletRadius = 0
  Length = 203.918
  MakeFace = true
  Placement = pos=(7800,0,6900) rot=(0,1,0;1.1781rad)
  Points = (2) [(0,0,0),(188.396,-5.76796e-15,-78.0361)]
  Start = (7800,0,6900)
  Subdivisions = 0
FEATURE [Part::Part2DObjectPython] Line109  # Draft 2D object (typed FeaturePython)
  ChamferSize = 0
  Closed = false
  End = (10410.7,0,5610.7)
  FilletRadius = 0
  Length = 1440.58
  MakeFace = false
  Placement = pos=(1741.79,0,-2756.57) rot=(0,-1,0;0.392699rad)
  Points = (2) [(11492.1,0,3000),(11211,0,4412.9)]
  Start = (11211,0,4412.9)
  Subdivisions = 0
FEATURE [Part::Part2DObjectPython] Line110  # Draft 2D object (typed FeaturePython)
  ChamferSize = 0
  Closed = false
  End = (10557.7,0,5757.72)
  FilletRadius = 0
  Length = 1521.7
  MakeFace = false
  Placement = pos=(1741.79,0,-2756.57) rot=(0,-1,0;0.392699rad)
  Points = (2) [(11700,0,3000),(11403.1,0,4492.47)]
  Start = (11403.1,0,4492.47)
  Subdivisions = 0
FEATURE [Part::Part2DObjectPython] Line111  # Draft 2D object (typed FeaturePython)
  ChamferSize = 0
  Closed = false
  End = (11214.7,6.2e-15,4414.43)
  FilletRadius = 0
  Length = 203.918
  MakeFace = true
  Placement = pos=(11403.1,0,4492.47) rot=(0,-1,0;0.392699rad)
  Points = (2) [(0,0,0),(-203.918,6.2432e-15,1.81899e-12)]
  Start = (11403.1,0,4492.47)
  Subdivisions = 0
FEATURE [Part::Part2DObjectPython] Line112  # Draft 2D object (typed FeaturePython)
  ChamferSize = 0
  Closed = false
  End = (9212.9,0,6411.04)
  FilletRadius = 0
  Length = 1440.58
  MakeFace = false
  Placement = pos=(4405.89,0,-4636.75) rot=(0,-1,0;0.785398rad)
  Points = (2) [(11492.1,0,3000),(11211,0,4412.9)]
  Start = (10410.7,0,5610.7)
  Subdivisions = 0
FEATURE [Part::Part2DObjectPython] Line113  # Draft 2D object (typed FeaturePython)
  ChamferSize = 0
  Closed = false
  End = (9292.47,0,6603.13)
  FilletRadius = 0
  Length = 1521.7
  MakeFace = false
  Placement = pos=(4405.89,0,-4636.75) rot=(0,-1,0;0.785398rad)
  Points = (2) [(11700,0,3000),(11403.1,0,4492.47)]
  Start = (10557.7,0,5757.72)
  Subdivisions = 0
FEATURE [Part::Part2DObjectPython] Line114  # Draft 2D object (typed FeaturePython)
  ChamferSize = 0
  Closed = false
  End = (10413.5,6.2e-15,5613.52)
  FilletRadius = 0
  Length = 203.918
  MakeFace = true
  Placement = pos=(10557.7,0,5757.72) rot=(0,-1,0;0.785398rad)
  Points = (2) [(0,0,0),(-203.918,6.2432e-15,1.36424e-12)]
  Start = (10557.7,0,5757.72)
  Subdivisions = 0
FEATURE [Part::Part2DObjectPython] Line115  # Draft 2D object (typed FeaturePython)
  ChamferSize = 0
  Closed = false
  End = (7800,0,6692.09)
  FilletRadius = 0
  Length = 1440.58
  MakeFace = false
  Placement = pos=(7586.71,0,-5354.31) rot=(0,-1,0;1.1781rad)
  Points = (2) [(11492.1,0,3000),(11211,0,4412.9)]
  Start = (9212.9,0,6411.04)
  Subdivisions = 0
FEATURE [Part::Part2DObjectPython] Line116  # Draft 2D object (typed FeaturePython)
  ChamferSize = 0
  Closed = false
  End = (7800,0,6900)
  FilletRadius = 0
  Length = 1521.7
  MakeFace = false
  Placement = pos=(7586.71,0,-5354.31) rot=(0,-1,0;1.1781rad)
  Points = (2) [(11700,0,3000),(11403.1,0,4492.47)]
  Start = (9292.47,0,6603.13)
  Subdivisions = 0
FEATURE [Part::Part2DObjectPython] Line117  # Draft 2D object (typed FeaturePython)
  ChamferSize = 0
  Closed = false
  End = (9214.43,6.2e-15,6414.73)
  FilletRadius = 0
  Length = 203.918
  MakeFace = true
  Placement = pos=(9292.47,0,6603.13) rot=(0,-1,0;1.1781rad)
  Points = (2) [(0,0,0),(-203.918,6.2432e-15,1.81899e-12)]
  Start = (9292.47,0,6603.13)
  Subdivisions = 0
FEATURE [Part::Part2DObjectPython] Line118  # Draft 2D object (typed FeaturePython)
  ChamferSize = 0
  Closed = false
  End = (3877.4,1606.07,4492.47)
  FilletRadius = 0
  Length = 1521.7
  MakeFace = false
  Placement = pos=(0,0,0) rot=(0,0,1;0.392699rad)
  Points = (2) [(3900,-2.27374e-13,3000),(4196.87,-2.27374e-13,4492.47)]
  Start = (3603.13,1492.47,3000)
  Subdivisions = 0
FEATURE [Part::Part2DObjectPython] Line119  # Draft 2D object (typed FeaturePython)
  ChamferSize = 0
  Closed = false
  End = (3791.53,1570.5,3000)
  FilletRadius = 0
  Length = 203.918
  MakeFace = true
  Placement = pos=(3603.13,1492.47,3000) rot=(0,0,1;0.392699rad)
  Points = (2) [(0,0,0),(203.918,2.27374e-13,0)]
  Start = (3603.13,1492.47,3000)
  Subdivisions = 0
FEATURE [Part::Part2DObjectPython] Line120  # Draft 2D object (typed FeaturePython)
  ChamferSize = 0
  Closed = false
  End = (4054.87,1679.58,4412.9)
  FilletRadius = 0
  Length = 1440.58
  MakeFace = false
  Placement = pos=(0,0,0) rot=(0,0,1;0.392699rad)
  Points = (2) [(4107.91,0,3000),(4388.96,9.09495e-13,4412.9)]
  Start = (3795.22,1572.03,3000)
  Subdivisions = 0
FEATURE [Part::Part2DObjectPython] Line121  # Draft 2D object (typed FeaturePython)
  ChamferSize = 0
  Closed = false
  End = (4051.46,1678.17,4414.43)
  FilletRadius = 0
  Length = 203.918
  MakeFace = true
  Placement = pos=(3877.4,1606.07,4492.47) rot=(-0.139281,0.700215,0.700215;0.553564rad)
  Points = (2) [(0,0,0),(203.918,-2.16594e-15,0)]
  Start = (3877.4,1606.07,4492.47)
  Subdivisions = 0
FEATURE [Part::Part2DObjectPython] Line122  # Draft 2D object (typed FeaturePython)
  ChamferSize = 0
  Closed = false
  End = (4658.46,1929.6,5757.72)
  FilletRadius = 0
  Length = 1521.7
  MakeFace = false
  Placement = pos=(-512.116,-212.126,3213.29) rot=(-0.139281,0.700215,0.700215;0.553564rad)
  Points = (2) [(3900,1.11194e-12,3000),(4196.87,6.28681e-14,4492.47)]
  Start = (3877.4,1606.07,4492.47)
  Subdivisions = 0
FEATURE [Part::Part2DObjectPython] Line124  # Draft 2D object (typed FeaturePython)
  ChamferSize = 0
  Closed = false
  End = (4791.68,1984.78,5613.52)
  FilletRadius = 0
  Length = 203.918
  MakeFace = true
  Placement = pos=(4658.46,1929.6,5757.72) rot=(-0.176494,0.887296,0.426094;0.873518rad)
  Points = (2) [(0,0,0),(203.918,8.89484e-13,0)]
  Start = (4658.46,1929.6,5757.72)
  Subdivisions = 0
FEATURE [Part::Part2DObjectPython] Line125  # Draft 2D object (typed FeaturePython)
  ChamferSize = 0
  Closed = false
  End = (5827.4,2413.79,6603.13)
  FilletRadius = 0
  Length = 1521.7
  MakeFace = false
  Placement = pos=(150.82,62.4718,6394.11) rot=(-0.176494,0.887296,0.426094;0.873518rad)
  Points = (2) [(3900,1.7662e-12,3000),(4196.87,5.19282e-13,4492.47)]
  Start = (4658.46,1929.6,5757.72)
  Subdivisions = 0
FEATURE [Part::Part2DObjectPython] Line126  # Draft 2D object (typed FeaturePython)
  ChamferSize = 0
  Closed = false
  End = (5900.91,2444.24,6411.04)
  FilletRadius = 0
  Length = 1440.58
  MakeFace = false
  Placement = pos=(150.82,62.4718,6394.11) rot=(-0.176494,0.887296,0.426094;0.873518rad)
  Points = (2) [(4107.91,1.51842e-12,3000),(4388.96,2.76636e-12,4412.9)]
  Start = (4794.29,1985.86,5610.7)
  Subdivisions = 0
FEATURE [Part::Part2DObjectPython] Line127  # Draft 2D object (typed FeaturePython)
  ChamferSize = 0
  Closed = false
  End = (5899.5,2443.65,6414.73)
  FilletRadius = 0
  Length = 203.918
  MakeFace = true
  Placement = pos=(5827.4,2413.79,6603.13) rot=(-0.176494,0.887296,0.426094;0.873518rad)
  Points = (2) [(0,0,0),(188.396,-5.22904e-15,-78.0361)]
  Start = (5827.4,2413.79,6603.13)
  Subdivisions = 0
FEATURE [Part::Part2DObjectPython] Line128  # Draft 2D object (typed FeaturePython)
  ChamferSize = 0
  Closed = false
  End = (7206.26,2984.93,6900)
  FilletRadius = 0
  Length = 1521.7
  MakeFace = false
  Placement = pos=(1887.88,781.987,9058.21) rot=(-0.187271,0.941476,0.280271;1.23443rad)
  Points = (2) [(3900,5.00292e-13,3000),(4196.87,-4.00963e-13,4492.47)]
  Start = (5827.4,2413.79,6603.13)
  Subdivisions = 0
FEATURE [Part::Part2DObjectPython] Line129  # Draft 2D object (typed FeaturePython)
  ChamferSize = 0
  Closed = false
  End = (7206.26,2984.93,6692.09)
  FilletRadius = 0
  Length = 1440.58
  MakeFace = false
  Placement = pos=(1887.88,781.987,9058.21) rot=(-0.187271,0.941476,0.280271;1.23443rad)
  Points = (2) [(4107.91,-4.14534e-13,3000),(4388.96,-8.61481e-13,4412.9)]
  Start = (5900.91,2444.24,6411.04)
  Subdivisions = 0
FEATURE [Part::Part2DObjectPython] Line130  # Draft 2D object (typed FeaturePython)
  ChamferSize = 0
  Closed = false
  End = (7206.26,2984.93,6696.08)
  FilletRadius = 0
  Length = 203.918
  MakeFace = true
  Placement = pos=(7206.26,2984.93,6900) rot=(-0.187271,0.941476,0.280271;1.23443rad)
  Points = (2) [(0,0,0),(188.396,0,-78.0361)]
  Start = (7206.26,2984.93,6900)
  Subdivisions = 0
FEATURE [Part::Part2DObjectPython] Line131  # Draft 2D object (typed FeaturePython)
  ChamferSize = 0
  Closed = false
  End = (7206.26,2984.93,6900)
  FilletRadius = 0
  Length = 1521.7
  MakeFace = false
  Placement = pos=(7009.2,2903.31,-5354.31) rot=(0.187271,-0.941476,0.280271;1.23443rad)
  Points = (2) [(11700,1.94185e-12,3000),(11403.1,-7.94873e-13,4492.47)]
  Start = (8585.12,3556.07,6603.13)
  Subdivisions = 0
FEATURE [Part::Part2DObjectPython] Line132  # Draft 2D object (typed FeaturePython)
  ChamferSize = 0
  Closed = false
  End = (7206.26,2984.93,6692.09)
  FilletRadius = 0
  Length = 1440.58
  MakeFace = false
  Placement = pos=(7009.2,2903.31,-5354.31) rot=(0.187271,-0.941476,0.280271;1.23443rad)
  Points = (2) [(11492.1,2.40193e-12,3000),(11211,1.20393e-13,4412.9)]
  Start = (8511.61,3525.62,6411.04)
  Subdivisions = 0
FEATURE [Part::Part2DObjectPython] Line133  # Draft 2D object (typed FeaturePython)
  ChamferSize = 0
  Closed = false
  End = (8513.02,3526.21,6414.73)
  FilletRadius = 0
  Length = 203.918
  MakeFace = true
  Placement = pos=(8585.12,3556.07,6603.13) rot=(0.187271,-0.941476,0.280271;1.23443rad)
  Points = (2) [(0,0,0),(-203.918,1.04581e-14,1.81899e-12)]
  Start = (8585.12,3556.07,6603.13)
  Subdivisions = 0
FEATURE [Part::Part2DObjectPython] Line134  # Draft 2D object (typed FeaturePython)
  ChamferSize = 0
  Closed = false
  End = (8585.12,3556.07,6603.13)
  FilletRadius = 0
  Length = 1521.7
  MakeFace = false
  Placement = pos=(4070.51,1686.06,-4636.75) rot=(0.176494,-0.887296,0.426094;0.873518rad)
  Points = (2) [(11700,7.77551e-13,3000),(11403.1,-1.285e-12,4492.47)]
  Start = (9754.06,4040.26,5757.72)
  Subdivisions = 0
FEATURE [Part::Part2DObjectPython] Line135  # Draft 2D object (typed FeaturePython)
  ChamferSize = 0
  Closed = false
  End = (8511.61,3525.62,6411.04)
  FilletRadius = 0
  Length = 1440.58
  MakeFace = false
  Placement = pos=(4070.51,1686.06,-4636.75) rot=(0.176494,-0.887296,0.426094;0.873518rad)
  Points = (2) [(11492.1,-1.68669e-13,3000),(11211,9.40752e-13,4412.9)]
  Start = (9618.23,3984,5610.7)
  Subdivisions = 0
FEATURE [Part::Part2DObjectPython] Line136  # Draft 2D object (typed FeaturePython)
  ChamferSize = 0
  Closed = false
  End = (9754.06,4040.26,5757.72)
  FilletRadius = 0
  Length = 1521.7
  MakeFace = false
  Placement = pos=(1609.2,666.554,-2756.57) rot=(0.139281,-0.700215,0.700215;0.553564rad)
  Points = (2) [(11700,6.88664e-12,3000),(11403.1,6.79885e-12,4492.47)]
  Start = (10535.1,4363.79,4492.47)
  Subdivisions = 0
FEATURE [Part::Part2DObjectPython] Line137  # Draft 2D object (typed FeaturePython)
  ChamferSize = 0
  Closed = false
  End = (9620.84,3985.08,5613.52)
  FilletRadius = 0
  Length = 203.918
  MakeFace = true
  Placement = pos=(9754.06,4040.26,5757.72) rot=(0.176494,-0.887296,0.426094;0.873518rad)
  Points = (2) [(0,0,0),(-203.918,1.32822e-12,1.36424e-12)]
  Start = (9754.06,4040.26,5757.72)
  Subdivisions = 0
FEATURE [Part::Part2DObjectPython] Line138  # Draft 2D object (typed FeaturePython)
  ChamferSize = 0
  Closed = false
  End = (9618.23,3984,5610.7)
  FilletRadius = 0
  Length = 1440.58
  MakeFace = false
  Placement = pos=(1609.2,666.554,-2756.57) rot=(0.139281,-0.700215,0.700215;0.553564rad)
  Points = (2) [(11492.1,5.07317e-12,3000),(11211,3.17107e-12,4412.9)]
  Start = (10357.7,4290.28,4412.9)
  Subdivisions = 0
FEATURE [Part::Part2DObjectPython] Line139  # Draft 2D object (typed FeaturePython)
  ChamferSize = 0
  Closed = false
  End = (10535.1,4363.79,4492.47)
  FilletRadius = 0
  Length = 1521.7
  MakeFace = false
  Placement = pos=(0,0,0) rot=(0,0,1;0.392699rad)
  Points = (2) [(11700,0,3000),(11403.1,-4.54747e-13,4492.47)]
  Start = (10809.4,4477.4,3000)
  Subdivisions = 0
FEATURE [Part::Part2DObjectPython] Line140  # Draft 2D object (typed FeaturePython)
  ChamferSize = 0
  Closed = false
  End = (10357.7,4290.28,4412.9)
  FilletRadius = 0
  Length = 1440.58
  MakeFace = false
  Placement = pos=(0,0,0) rot=(0,0,1;0.392699rad)
  Points = (2) [(11492.1,-4.54747e-13,3000),(11211,0,4412.9)]
  Start = (10617.3,4397.83,3000)
  Subdivisions = 0
FEATURE [Part::Part2DObjectPython] Line141  # Draft 2D object (typed FeaturePython)
  ChamferSize = 0
  Closed = false
  End = (10361.1,4291.69,4414.43)
  FilletRadius = 0
  Length = 203.918
  MakeFace = true
  Placement = pos=(10535.1,4363.79,4492.47) rot=(0,0,1;0.392699rad)
  Points = (2) [(0,0,0),(-188.396,0,-78.0361)]
  Start = (10535.1,4363.79,4492.47)
  Subdivisions = 0
FEATURE [Part::Part2DObjectPython] Line142  # Draft 2D object (typed FeaturePython)
  ChamferSize = 0
  Closed = false
  End = (10621,4399.36,3000)
  FilletRadius = 0
  Length = 203.918
  MakeFace = true
  Placement = pos=(10809.4,4477.4,3000) rot=(0,0,1;0.392699rad)
  Points = (2) [(0,0,0),(-203.918,1.36424e-12,0)]
  Start = (10809.4,4477.4,3000)
  Subdivisions = 0
FEATURE [Part::Part2DObjectPython] Line143  # Draft 2D object (typed FeaturePython)
  ChamferSize = 0
  Closed = false
  End = (10809.4,4477.4,3000)
  FilletRadius = 0
  Length = 4565.11
  MakeFace = true
  Placement = pos=(11700,0,3000) rot=(0,0,1;0rad)
  Points = (2) [(0,0,0),(-890.609,4477.4,0)]
  Start = (11700,0,3000)
  Subdivisions = 0
FEATURE [Part::Part2DObjectPython] Line144  # Draft 2D object (typed FeaturePython)
  ChamferSize = 0
  Closed = false
  End = (10535.1,4363.79,4492.47)
  FilletRadius = 0
  Length = 4449.28
  MakeFace = true
  Placement = pos=(11403.1,0,4492.47) rot=(0,0,1;0rad)
  Points = (2) [(0,0,0),(-868.012,4363.79,0)]
  Start = (11403.1,0,4492.47)
  Subdivisions = 0
FEATURE [Part::Part2DObjectPython] Line145  # Draft 2D object (typed FeaturePython)
  ChamferSize = 0
  Closed = false
  End = (9754.06,4040.26,5757.72)
  FilletRadius = 0
  Length = 4119.42
  MakeFace = true
  Placement = pos=(10557.7,0,5757.72) rot=(0,0,1;0rad)
  Points = (2) [(0,0,0),(-803.658,4040.26,-1.81899e-12)]
  Start = (10557.7,0,5757.72)
  Subdivisions = 0
FEATURE [Part::Part2DObjectPython] Line146  # Draft 2D object (typed FeaturePython)
  ChamferSize = 0
  Closed = false
  End = (8585.12,3556.07,6603.13)
  FilletRadius = 0
  Length = 3625.74
  MakeFace = true
  Placement = pos=(9292.47,0,6603.13) rot=(0,0,1;0rad)
  Points = (2) [(0,0,0),(-707.347,3556.07,-1.54614e-11)]
  Start = (9292.47,0,6603.13)
  Subdivisions = 0
FEATURE [Part::Part2DObjectPython] Line147  # Draft 2D object (typed FeaturePython)
  ChamferSize = 0
  Closed = false
  End = (7206.26,2984.93,6900)
  FilletRadius = 0
  Length = 3043.41
  MakeFace = true
  Placement = pos=(7800,0,6900) rot=(0,0,1;0rad)
  Points = (2) [(0,0,0),(-593.74,2984.93,-1.27329e-11)]
  Start = (7800,0,6900)
  Subdivisions = 0
FEATURE [Part::Part2DObjectPython] Line148  # Draft 2D object (typed FeaturePython)
  ChamferSize = 0
  Closed = false
  End = (5827.4,2413.79,6603.13)
  FilletRadius = 0
  Length = 2461.08
  MakeFace = true
  Placement = pos=(6307.53,0,6603.13) rot=(0,0,1;0rad)
  Points = (2) [(0,0,0),(-480.132,2413.79,0)]
  Start = (6307.53,0,6603.13)
  Subdivisions = 0
FEATURE [Part::Part2DObjectPython] Line149  # Draft 2D object (typed FeaturePython)
  ChamferSize = 0
  Closed = false
  End = (4658.46,1929.6,5757.72)
  FilletRadius = 0
  Length = 1967.4
  MakeFace = true
  Placement = pos=(5042.28,0,5757.72) rot=(0,0,1;0rad)
  Points = (2) [(0,0,0),(-383.821,1929.6,2.72848e-12)]
  Start = (5042.28,0,5757.72)
  Subdivisions = 0
FEATURE [Part::Part2DObjectPython] Line150  # Draft 2D object (typed FeaturePython)
  ChamferSize = 0
  Closed = false
  End = (3877.4,1606.07,4492.47)
  FilletRadius = 0
  Length = 1637.54
  MakeFace = true
  Placement = pos=(4196.87,0,4492.47) rot=(0,0,1;0rad)
  Points = (2) [(0,0,0),(-319.468,1606.07,3.63798e-12)]
  Start = (4196.87,0,4492.47)
  Subdivisions = 0
FEATURE [Part::Part2DObjectPython] Line151  # Draft 2D object (typed FeaturePython)
  ChamferSize = 0
  Closed = false
  End = (5189.3,0,5610.7)
  FilletRadius = 0
  Length = 1441.37
  MakeFace = true
  Placement = pos=(4385.27,0,4414.43) rot=(0,0,1;0rad)
  Points = (2) [(0,0,0),(804.035,-2.46165e-14,1196.27)]
  Start = (4385.27,0,4414.43)
  Subdivisions = 0
FEATURE [Part::Part2DObjectPython] Line152  # Draft 2D object (typed FeaturePython)
  ChamferSize = 0
  Closed = false
  End = (4794.29,1985.86,5610.7)
  FilletRadius = 0
  Length = 1441.37
  MakeFace = true
  Placement = pos=(4051.46,1678.17,4414.43) rot=(0,0,1;0rad)
  Points = (2) [(0,0,0),(742.831,307.691,1196.27)]
  Start = (4051.46,1678.17,4414.43)
  Subdivisions = 0
FEATURE [Part::Part2DObjectPython] Line153  # Draft 2D object (typed FeaturePython)
  ChamferSize = 0
  Closed = false
  End = (3603.13,-1500,4492.47)
  FilletRadius = 0
  Length = 1521.7
  MakeFace = true
  Placement = pos=(3900,-1500,3000) rot=(0,0,1;0rad)
  Points = (2) [(0,0,0),(-296.87,9.09495e-13,1492.47)]
  Start = (3900,-1500,3000)
  Subdivisions = 0
FEATURE [Part::Part2DObjectPython] Line154  # Draft 2D object (typed FeaturePython)
  ChamferSize = 0
  Closed = false
  End = (3603.13,0,4492.47)
  FilletRadius = 0
  Length = 1500
  MakeFace = true
  Placement = pos=(3603.13,-1500,4492.47) rot=(0,0,1;0rad)
  Points = (2) [(0,0,0),(0,1500,0)]
  Start = (3603.13,-1500,4492.47)
  Subdivisions = 0
FEATURE [Part::Feature] Fusion014  label="H003"
  Placement = pos=(7800,-750,0) rot=(0.19148,-0.962637,0.19148;1.60886rad)
  shape: bbox 100 x 100 x 3035 mm, 4 faces (baked)
FEATURE [Part::Cylinder] Cylinder003  label="Цилиндр003"
  Angle = 360
  AttacherType = Attacher::AttachEngine3D
  Height = 3700
  Placement = pos=(0,0,0) rot=(0,1,0;1.5708rad)
  Radius = 25
FEATURE [Part::Cone] Cone004  label="Конус004"
  Angle = 360
  AttacherType = Attacher::AttachEngine3D
  Height = 200
  Placement = pos=(3700,0,0) rot=(0,1,0;1.5708rad)
  Radius1 = 50
  Radius2 = 0
FEATURE [Part::MultiFuse] Fusion015  label="OR*2"
  Placement = pos=(3900,-750,0) rot=(0,0,1;0rad)
  Refine = true
  Shapes = -> [Cylinder003,Cone004]
FEATURE [Part::Feature] Fusion016  label="OR*003"
  Placement = pos=(7800,-750,0) rot=(0,0,1;0rad)
  shape: bbox 3900 x 100 x 100 mm, 4 faces (baked)
FEATURE [Part::Part2DObjectPython] Line155  # Draft 2D object (typed FeaturePython)
  ChamferSize = 0
  Closed = false
  End = (7800,-750,3000)
  FilletRadius = 0
  Length = 3900
  MakeFace = true
  Placement = pos=(3900,-750,3000) rot=(0,0,1;0rad)
  Points = (2) [(0,0,0),(3900,2.27374e-13,4.54747e-13)]
  Start = (3900,-750,3000)
  Subdivisions = 0
FEATURE [Part::Part2DObjectPython] Line156  # Draft 2D object (typed FeaturePython)
  ChamferSize = 0
  Closed = false
  End = (11700,-750,3000)
  FilletRadius = 0
  Length = 3900
  MakeFace = true
  Placement = pos=(7800,-750,3000) rot=(0,0,1;0rad)
  Points = (2) [(0,0,0),(3900,2.27374e-13,4.54747e-13)]
  Start = (7800,-750,3000)
  Subdivisions = 0
FEATURE [Part::Part2DObjectPython] Line157  # Draft 2D object (typed FeaturePython)
  ChamferSize = 0
  Closed = false
  End = (11700,0,0)
  FilletRadius = 0
  Length = 3000
  MakeFace = true
  Placement = pos=(11700,0,3000) rot=(0,0,1;0rad)
  Points = (2) [(0,0,0),(0,0,-3000)]
  Start = (11700,0,3000)
  Subdivisions = 0
FEATURE [Part::Feature] Fusion017  label="TORSION004"
  Placement = pos=(7800,-750,3000) rot=(0,0.707107,0.707107;3.14159rad)
  shape: bbox 1558 x 100 x 1579 mm, 4 faces (baked)
FEATURE [Part::Part2DObjectPython] Line162  # Draft 2D object (typed FeaturePython)
  ChamferSize = 0
  Closed = false
  End = (7800,-750,6900)
  FilletRadius = 0
  Length = 3900
  MakeFace = true
  Placement = pos=(7800,-750,3000) rot=(0.707107,0,0.707107;3.14159rad)
  Points = (2) [(0,0,0),(3900,2.27374e-13,3.63798e-12)]
  Start = (7800,-750,3000)
  Subdivisions = 0
FEATURE [Part::Part2DObjectPython] Line163  # Draft 2D object (typed FeaturePython)
  ChamferSize = 0
  Closed = false
  End = (6307.53,-750,6603.13)
  FilletRadius = 0
  Length = 3900
  MakeFace = true
  Placement = pos=(7800,-750,3000) rot=(0.55557,0,0.83147;3.14159rad)
  Points = (2) [(0,0,0),(3900,2.27374e-13,5.45697e-12)]
  Start = (7800,-750,3000)
  Subdivisions = 0
FEATURE [Part::Part2DObjectPython] Line164  # Draft 2D object (typed FeaturePython)
  ChamferSize = 0
  Closed = false
  End = (5042.28,-750,5757.72)
  FilletRadius = 0
  Length = 3900
  MakeFace = true
  Placement = pos=(7800,-750,3000) rot=(0.382683,0,0.92388;3.14159rad)
  Points = (2) [(0,0,0),(3900,2.27374e-13,0)]
  Start = (7800,-750,3000)
  Subdivisions = 0
FEATURE [Part::Part2DObjectPython] Line165  # Draft 2D object (typed FeaturePython)
  ChamferSize = 0
  Closed = false
  End = (4196.87,-750,4492.47)
  FilletRadius = 0
  Length = 3900
  MakeFace = true
  Placement = pos=(7800,-750,3000) rot=(0.19509,0,0.980785;3.14159rad)
  Points = (2) [(0,0,0),(3900,2.27374e-13,0)]
  Start = (7800,-750,3000)
  Subdivisions = 0
FEATURE [Part::Part2DObjectPython] Line166  # Draft 2D object (typed FeaturePython)
  ChamferSize = 0
  Closed = false
  End = (-3900,-1.3642e-12,0)
  FilletRadius = 0
  Length = 3900
  MakeFace = true
  Placement = pos=(0,0,0) rot=(0,0,1;2.74889rad)
  Points = (2) [(0,0,0),(3603.13,1492.47,0)]
  Start = (0,0,0)
  Subdivisions = 0
FEATURE [Part::Part2DObjectPython] Line167  # Draft 2D object (typed FeaturePython)
  ChamferSize = 0
  Closed = false
  End = (3.416e-13,-1.616e-12,7900)
  FilletRadius = 0
  Length = 1000
  MakeFace = true
  Placement = pos=(3.11e-13,-1.616e-12,6900) rot=(1,0,0;1.5708rad)
  Points = (2) [(0,0,0),(3.06162e-14,1000,2.22045e-13)]
  Start = (3.11e-13,-1.616e-12,6900)
  Subdivisions = 0
FEATURE [Part::Part2DObjectPython] Line168  # Draft 2D object (typed FeaturePython)
  ChamferSize = 0
  Closed = false
  End = (7800,0,7900)
  FilletRadius = 0
  Length = 1000
  MakeFace = true
  Placement = pos=(7800,0,6900) rot=(1,0,0;1.5708rad)
  Points = (2) [(0,0,0),(0,1000,2.22045e-13)]
  Start = (7800,0,6900)
  Subdivisions = 0
FEATURE [Part::Part2DObjectPython] Line169  # Draft 2D object (typed FeaturePython)
  ChamferSize = 0
  Closed = false
  End = (7206.26,2984.93,7900)
  FilletRadius = 0
  Length = 1000
  MakeFace = true
  Placement = pos=(7206.26,2984.93,6900) rot=(1,0,0;1.5708rad)
  Points = (2) [(0,0,0),(0,1000,1.36424e-12)]
  Start = (7206.26,2984.93,6900)
  Subdivisions = 0
FEATURE [Part::Part2DObjectPython] Line170  # Draft 2D object (typed FeaturePython)
  ChamferSize = 0
  Closed = false
  End = (1492.47,0,7103.13)
  FilletRadius = 0
  Length = 500
  MakeFace = true
  Placement = pos=(1492.47,0,6603.13) rot=(1,0,0;1.5708rad)
  Points = (2) [(0,0,0),(0,500,1.11022e-13)]
  Start = (1492.47,0,6603.13)
  Subdivisions = 0
FEATURE [Part::Part2DObjectPython] Line171  # Draft 2D object (typed FeaturePython)
  ChamferSize = 0
  Closed = false
  End = (6307.53,0,7103.13)
  FilletRadius = 0
  Length = 500
  MakeFace = true
  Placement = pos=(6307.53,0,6603.13) rot=(1,0,0;1.5708rad)
  Points = (2) [(0,0,0),(0,500,1.11022e-13)]
  Start = (6307.53,0,6603.13)
  Subdivisions = 0
FEATURE [Part::Part2DObjectPython] Line172  # Draft 2D object (typed FeaturePython)
  ChamferSize = 0
  Closed = false
  End = (5827.4,2413.79,7103.13)
  FilletRadius = 0
  Length = 500
  MakeFace = true
  Placement = pos=(5827.4,2413.79,6603.13) rot=(1,0,0;1.5708rad)
  Points = (2) [(0,0,0),(0,500,0)]
  Start = (5827.4,2413.79,6603.13)
  Subdivisions = 0
FEATURE [Part::Part2DObjectPython] Line173  # Draft 2D object (typed FeaturePython)
  ChamferSize = 0
  Closed = false
  End = (8585.12,3556.07,7103.13)
  FilletRadius = 0
  Length = 500
  MakeFace = true
  Placement = pos=(8585.12,3556.07,6603.13) rot=(1,0,0;1.5708rad)
  Points = (2) [(0,0,0),(0,500,0)]
  Start = (8585.12,3556.07,6603.13)
  Subdivisions = 0
FEATURE [Part::Part2DObjectPython] Line174  # Draft 2D object (typed FeaturePython)
  ChamferSize = 0
  Closed = false
  End = (9292.47,5.66e-13,7103.13)
  FilletRadius = 0
  Length = 500
  MakeFace = true
  Placement = pos=(9292.47,4.55e-13,6603.13) rot=(1,0,0;1.5708rad)
  Points = (2) [(0,0,0),(0,500,0)]
  Start = (9292.47,4.55e-13,6603.13)
  Subdivisions = 0
FEATURE [Part::Part2DObjectPython] Line175  # Draft 2D object (typed FeaturePython)
  ChamferSize = 0
  Closed = false
  End = (1378.86,571.142,7103.13)
  FilletRadius = 0
  Length = 500
  MakeFace = true
  Placement = pos=(1378.86,571.142,6603.13) rot=(1,0,0;1.5708rad)
  Points = (2) [(0,0,0),(0,500,1.13687e-13)]
  Start = (1378.86,571.142,6603.13)
  Subdivisions = 0
FEATURE [Part::Part2DObjectPython] Line176  # Draft 2D object (typed FeaturePython)
  ChamferSize = 0
  Closed = false
  End = (3900,0,7900)
  FilletRadius = 0
  Length = 4900
  MakeFace = true
  Placement = pos=(3900,0,3000) rot=(1,0,0;1.5708rad)
  Points = (2) [(0,0,0),(1.81899e-12,4900,1.08802e-12)]
  Start = (3900,0,3000)
  Subdivisions = 0
FEATURE [Part::Part2DObjectPython] Line177  # Draft 2D object (typed FeaturePython)
  ChamferSize = 0
  Closed = false
  End = (3603.13,1492.47,7900)
  FilletRadius = 0
  Length = 4900
  MakeFace = true
  Placement = pos=(3603.13,1492.47,3000) rot=(1,0,0;1.5708rad)
  Points = (2) [(0,0,0),(4.09273e-12,4900,1.13687e-12)]
  Start = (3603.13,1492.47,3000)
  Subdivisions = 0
FEATURE [Part::Part2DObjectPython] Line178  # Draft 2D object (typed FeaturePython)
  ChamferSize = 0
  Closed = false
  End = (7206.26,2984.93,7900)
  FilletRadius = 0
  Length = 7800
  MakeFace = true
  Placement = pos=(3.11e-13,-1.616e-12,7900) rot=(1,0,0;1.5708rad)
  Points = (2) [(0,0,0),(7206.26,-1.18234e-11,-2984.93)]
  Start = (3.11e-13,-1.616e-12,7900)
  Subdivisions = 0
FEATURE [Part::Part2DObjectPython] Line179  # Draft 2D object (typed FeaturePython)
  ChamferSize = 0
  Closed = false
  End = (7800,2.388e-13,7900)
  FilletRadius = 0
  Length = 7800
  MakeFace = true
  Placement = pos=(3.11e-13,-1.616e-12,7900) rot=(1,0,0;1.5708rad)
  Points = (2) [(0,0,0),(7800,9.09495e-13,-1.85485e-12)]
  Start = (3.11e-13,-1.616e-12,7900)
  Subdivisions = 0
FEATURE [Part::Part2DObjectPython] Line180  # Draft 2D object (typed FeaturePython)
  ChamferSize = 0
  Closed = false
  End = (9292.47,5.658e-13,7103.13)
  FilletRadius = 0
  Length = 7800
  MakeFace = true
  Placement = pos=(1492.47,0,7103.13) rot=(1,0,0;1.5708rad)
  Points = (2) [(0,0,0),(7800,4.54747e-12,-8.04576e-13)]
  Start = (1492.47,0,7103.13)
  Subdivisions = 0
FEATURE [Part::Part2DObjectPython] Line181  # Draft 2D object (typed FeaturePython)
  ChamferSize = 0
  Closed = false
  End = (8585.12,3556.07,7103.13)
  FilletRadius = 0
  Length = 7800
  MakeFace = true
  Placement = pos=(1378.86,571.142,7103.13) rot=(1,0,0;1.5708rad)
  Points = (2) [(0,0,0),(7206.26,-8.18545e-12,-2984.93)]
  Start = (1378.86,571.142,7103.13)
  Subdivisions = 0
FEATURE [Part::Part2DObjectPython] Line182  # Draft 2D object (typed FeaturePython)
  ChamferSize = 0
  Closed = false
  End = (11403.1,0,4492.47)
  FilletRadius = 0
  Length = 1500
  MakeFace = true
  Placement = pos=(11403.1,-1500,4492.47) rot=(0,0,1;0rad)
  Points = (2) [(0,0,0),(0,1500,0)]
  Start = (11403.1,-1500,4492.47)
  Subdivisions = 0
FEATURE [Part::Part2DObjectPython] Line183  # Draft 2D object (typed FeaturePython)
  ChamferSize = 0
  Closed = false
  End = (10557.7,6.821e-13,5757.72)
  FilletRadius = 0
  Length = 1500
  MakeFace = true
  Placement = pos=(10557.7,-1500,5757.72) rot=(0,-1,0;0.392699rad)
  Points = (2) [(0,0,0),(0,1500,0)]
  Start = (10557.7,-1500,5757.72)
  Subdivisions = 0
FEATURE [Part::Part2DObjectPython] Line184  # Draft 2D object (typed FeaturePython)
  ChamferSize = 0
  Closed = false
  End = (9292.47,1.3642e-12,6603.13)
  FilletRadius = 0
  Length = 1500
  MakeFace = true
  Placement = pos=(9292.47,-1500,6603.13) rot=(0,-1,0;0.785398rad)
  Points = (2) [(0,0,0),(0,1500,0)]
  Start = (9292.47,-1500,6603.13)
  Subdivisions = 0
FEATURE [Part::Part2DObjectPython] Line185  # Draft 2D object (typed FeaturePython)
  ChamferSize = 0
  Closed = false
  End = (7800,1.5916e-12,6900)
  FilletRadius = 0
  Length = 1500
  MakeFace = true
  Placement = pos=(7800,-1500,6900) rot=(0,-1,0;1.1781rad)
  Points = (2) [(0,0,0),(0,1500,0)]
  Start = (7800,-1500,6900)
  Subdivisions = 0
FEATURE [Part::Part2DObjectPython] Line186  # Draft 2D object (typed FeaturePython)
  ChamferSize = 0
  Closed = false
  End = (6307.53,2.7285e-12,6603.13)
  FilletRadius = 0
  Length = 1500
  MakeFace = true
  Placement = pos=(6307.53,-1500,6603.13) rot=(0,-1,0;1.5708rad)
  Points = (2) [(0,0,0),(0,1500,0)]
  Start = (6307.53,-1500,6603.13)
  Subdivisions = 0
FEATURE [Part::Part2DObjectPython] Line187  # Draft 2D object (typed FeaturePython)
  ChamferSize = 0
  Closed = false
  End = (5042.28,8.4128e-12,5757.72)
  FilletRadius = 0
  Length = 1500
  MakeFace = true
  Placement = pos=(5042.28,-1500,5757.72) rot=(0,-1,0;1.96349rad)
  Points = (2) [(0,0,0),(0,1500,0)]
  Start = (5042.28,-1500,5757.72)
  Subdivisions = 0
FEATURE [Part::Part2DObjectPython] Line188  # Draft 2D object (typed FeaturePython)
  ChamferSize = 0
  Closed = false
  End = (4196.87,1.84173e-11,4492.47)
  FilletRadius = 0
  Length = 1500
  MakeFace = true
  Placement = pos=(4196.87,-1500,4492.47) rot=(0,1,0;3.92699rad)
  Points = (2) [(0,0,0),(0,1500,0)]
  Start = (4196.87,-1500,4492.47)
  Subdivisions = 0
FEATURE [Part::Part2DObjectPython] Wire  # Draft 2D object (typed FeaturePython)
  ChamferSize = 0
  Closed = false
  End = (7800,-1500,6900)
  FilletRadius = 0
  Length = 4565.11
  MakeFace = true
  Placement = pos=(4196.87,-1500,4492.47) rot=(1,0,0;1.5708rad)
  Points = (4) [(0,0,0),(845.414,1265.25,2.27374e-13),(2110.66,2110.66,4.54747e-13),(3603.13,2407.53,1.36424e-12)]
  Start = (4196.87,-1500,4492.47)
  Subdivisions = 0
FEATURE [Part::Part2DObjectPython] Wire002  # Draft 2D object (typed FeaturePython)
  ChamferSize = 0
  Closed = false
  End = (11403.1,-1500,4492.47)
  FilletRadius = 0
  Length = 4565.11
  MakeFace = true
  Placement = pos=(7800,-1500,6900) rot=(0.726831,0.485653,-0.485653;1.88458rad)
  Points = (4) [(0,0,0),(845.414,1265.25,2.27374e-13),(2110.66,2110.66,4.54747e-13),(3603.13,2407.53,1.81899e-12)]
  Start = (7800,-1500,6900)
  Subdivisions = 0
FEATURE [Part::Part2DObjectPython] Line189  # Draft 2D object (typed FeaturePython)
  ChamferSize = 0
  Closed = false
  End = (10809.4,4477.4,-4.547e-13)
  FilletRadius = 0
  Length = 3000
  MakeFace = true
  Placement = pos=(10809.4,4477.4,3000) rot=(0,0,1;0.392699rad)
  Points = (2) [(0,0,0),(0,0,-3000)]
  Start = (10809.4,4477.4,3000)
  Subdivisions = 0
FEATURE [Part::Part2DObjectPython] Line190  # Draft 2D object (typed FeaturePython)
  ChamferSize = 0
  Closed = false
  End = (10621,4399.36,1500)
  FilletRadius = 0
  Length = 1500
  MakeFace = false
  Placement = pos=(0,0,0) rot=(0,0,1;0.392699rad)
  Points = (2) [(11496.1,-4.54747e-13,0),(11496.1,-4.54747e-13,1500)]
  Start = (10621,4399.36,0)
  Subdivisions = 0
FEATURE [Part::Part2DObjectPython] Line191  # Draft 2D object (typed FeaturePython)
  ChamferSize = 0
  Closed = false
  End = (10621,4399.36,1500)
  FilletRadius = 0
  Length = 4486.31
  MakeFace = true
  Placement = pos=(11500,0,1500) rot=(0,0,1;0rad)
  Points = (2) [(0,0,0),(-879.005,4399.36,0)]
  Start = (11500,0,1500)
  Subdivisions = 0
FEATURE [Part::Part2DObjectPython] Line192  # Draft 2D object (typed FeaturePython)
  ChamferSize = 0
  Closed = false
  End = (10809.4,4477.4,0)
  FilletRadius = 0
  Length = 4565.11
  MakeFace = true
  Placement = pos=(11700,0,0) rot=(0,0,1;0rad)
  Points = (2) [(0,0,0),(-890.609,4477.4,0)]
  Start = (11700,0,0)
  Subdivisions = 0
FEATURE [Part::Part2DObjectPython] Line193  # Draft 2D object (typed FeaturePython)
  ChamferSize = 0
  Closed = false
  End = (10809.4,4477.4,0)
  FilletRadius = 0
  Length = 203.918
  MakeFace = true
  Placement = pos=(10621,4399.36,0) rot=(0,0,1;0rad)
  Points = (2) [(0,0,0),(188.396,78.0361,0)]
  Start = (10621,4399.36,0)
  Subdivisions = 0
FEATURE [Part::Part2DObjectPython] Line194  # Draft 2D object (typed FeaturePython)
  ChamferSize = 0
  Closed = false
  End = (11500,0,0)
  FilletRadius = 0
  Length = 4486.31
  MakeFace = true
  Placement = pos=(10621,4399.36,0) rot=(0,0,1;0rad)
  Points = (2) [(0,0,0),(879.005,-4399.36,0)]
  Start = (10621,4399.36,0)
  Subdivisions = 0
FEATURE [Part::Part2DObjectPython] Line195  # Draft 2D object (typed FeaturePython)
  ChamferSize = 0
  Closed = false
  End = (10809.4,4477.4,1500)
  FilletRadius = 0
  Length = 203.918
  MakeFace = true
  Placement = pos=(10621,4399.36,1500) rot=(0,0,1;0rad)
  Points = (2) [(0,0,0),(188.396,78.0361,0)]
  Start = (10621,4399.36,1500)
  Subdivisions = 0
FEATURE [Part::Part2DObjectPython] Line196  # Draft 2D object (typed FeaturePython)
  ChamferSize = 0
  Closed = false
  End = (10809.4,4477.4,1500)
  FilletRadius = 0
  Length = 4565.11
  MakeFace = true
  Placement = pos=(11700,0,1500) rot=(0,0,1;0rad)
  Points = (2) [(0,0,0),(-890.609,4477.4,0)]
  Start = (11700,0,1500)
  Subdivisions = 0
FEATURE [Part::Part2DObjectPython] Arc001  # Draft 2D object (typed FeaturePython)
  FirstAngle = 180
  LastAngle = 360
  MakeFace = true
  Placement = pos=(7800,-750,0) rot=(0,0,1;0rad)
  Radius = 1400
FEATURE [Part::Part2DObjectPython] Circle  label="Circle003"  # Draft 2D object (typed FeaturePython)
  FirstAngle = 0
  LastAngle = 0
  MakeFace = true
  Placement = pos=(6400,-750,0) rot=(1,0,0;1.5708rad)
  Radius = 25
FEATURE [Part::Sweep] Sweep001
  Frenet = false
  Sections = -> [Circle]
  Solid = true
  Spine = -> Arc001 [Edge1]
  Transition = 1
FEATURE [Part::Cone] Cone005  label="Конус005"
  Angle = 360
  AttacherType = Attacher::AttachEngine3D
  Height = 200
  Placement = pos=(9187,-950,0) rot=(-1,0,0;1.5708rad)
  Radius1 = 50
  Radius2 = 0
FEATURE [Part::Box] Box001  label="Куб001"
  AttacherType = Attacher::AttachEngine3D
  Height = 60
  Length = 200
  Placement = pos=(9090,-950,-30) rot=(0,0,1;0rad)
  Width = 200
FEATURE [Part::Cut] Cut001
  Base = -> Sweep001
  Refine = true
  Tool = -> Box001
FEATURE [Part::MultiFuse] Fusion018
  Refine = true
  Shapes = -> [Cut001,Cone005]
